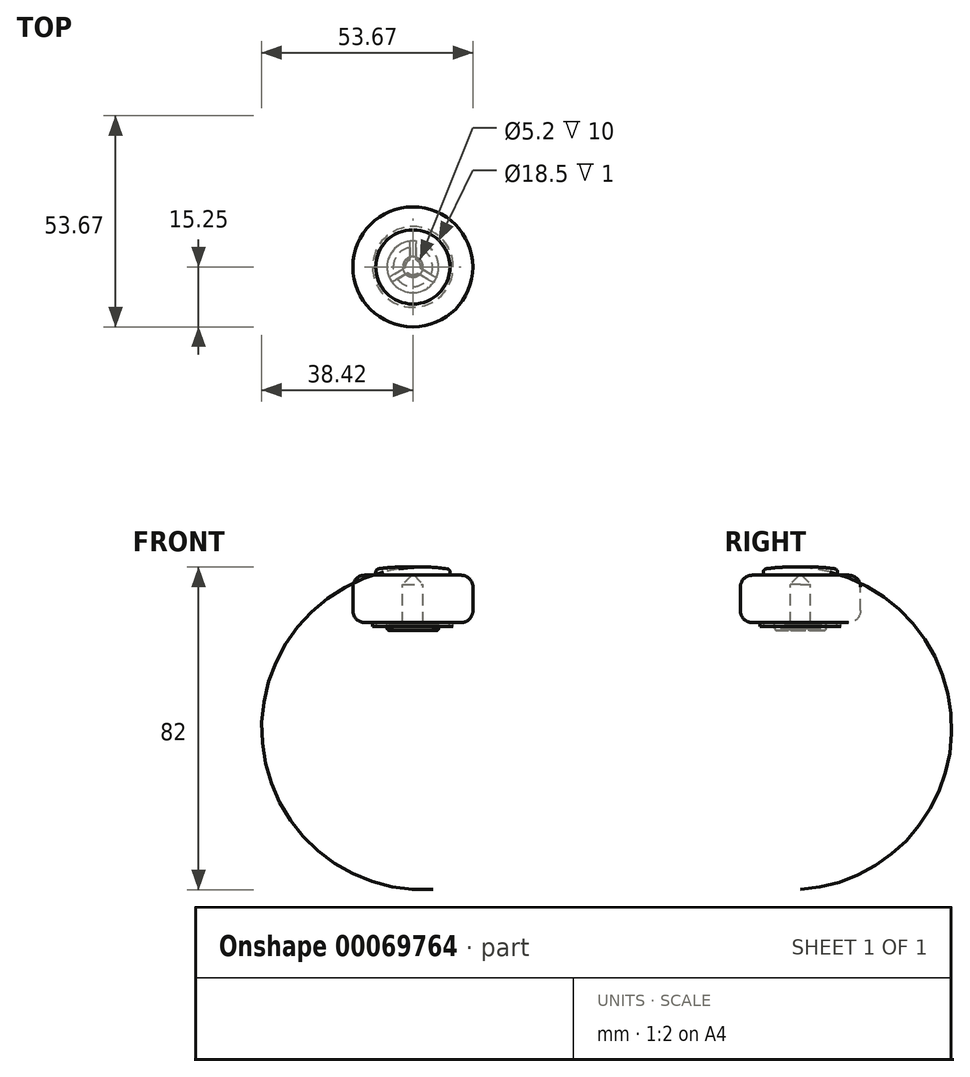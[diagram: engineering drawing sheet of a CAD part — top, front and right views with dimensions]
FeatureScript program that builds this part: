
annotation { "Feature Type Name" : "Feature", "Feature Type Description" : "" }
export const myFeature = defineFeature(function(context is Context, id is Id, definition is map)
    precondition{}
    {
        {
            var Q0;
            Q0=qCreatedBy(makeId("Right.planeOp"),FACE);
            var sketch = newSketch(context, id + "F0", { "sketchPlane" : qUnion([Q0])});
            skLineSegment(sketch, "E0", {"start": v(0, 18.3) * mm, "end": v(0, -9.78) * mm, "construction": true});
            skLineSegment(sketch, "E1", {"start": v(9.43, 2.55) * mm, "end": v(15.25, 2.55) * mm});
            skLineSegment(sketch, "E2", {"start": v(15.25, 2.55) * mm, "end": v(15.25, -9.46) * mm});
            skLineSegment(sketch, "E3", {"start": v(15.25, -9.46) * mm, "end": v(10.25, -9.46) * mm});
            skLineSegment(sketch, "E4", {"start": v(10.25, -9.46) * mm, "end": v(10.25, -10.46) * mm});
            skLineSegment(sketch, "E5", {"start": v(10.25, -10.46) * mm, "end": v(9.25, -10.46) * mm});
            skLineSegment(sketch, "E6", {"start": v(9.25, -10.46) * mm, "end": v(9.25, -9.46) * mm});
            skLineSegment(sketch, "E7", {"start": v(9.25, -9.46) * mm, "end": v(6.55, -9.46) * mm});
            skLineSegment(sketch, "E8", {"start": v(6.55, -9.46) * mm, "end": v(6.55, -11.46) * mm});
            skLineSegment(sketch, "E9", {"start": v(6.55, -11.46) * mm, "end": v(2.55, -11.46) * mm});
            skLineSegment(sketch, "E10", {"start": v(2.55, -11.46) * mm, "end": v(1.95, -9.78) * mm});
            skLineSegment(sketch, "E11", {"start": v(1.95, -9.78) * mm, "end": v(2.6, -9.78) * mm});
            skLineSegment(sketch, "E12", {"start": v(2.6, -9.78) * mm, "end": v(2.6, 0.22) * mm});
            skLineSegment(sketch, "E13", {"start": v(0, 2.82) * mm, "end": v(0, 4.54) * mm});
            skLineSegment(sketch, "E14", {"start": v(2.6, 0.22) * mm, "end": v(0, 2.82) * mm});
            skLineSegment(sketch, "E15", {"start": v(9.43, 2.55) * mm, "end": v(9.43, 4.05) * mm});
            skArc(sketch, "E16", {"start": v(9.43, 4.05) * mm, "mid": v(4.73, 4.57) * mm, "end": v(0, 4.54) * mm});
            skSolve(sketch);
        }
        {
            var Q0;
            Q0 = qSketchRegion(id + "F0", true);
            var Q1;
            Q1=sQuery(id+"F0.wireOp",EDGE,"E0");
            revolve(context, id + "F1", {"entities" : qUnion([Q0]), "axis" : qUnion([Q1]), "revolveType" : RevolveType.FULL});
        }
        {
            var Q0;
            Q0=makeQuery(id+"F1.opRevolve","SWEPT_FACE",FACE,{"disambiguationData":[OSD([sQuery(id+"F0.wireOp",EDGE,"E9")])]});
            var sketch = newSketch(context, id + "F2", { "sketchPlane" : qUnion([Q0])});
            skArc(sketch, "E17", {"start": v(-0.7, -6.51) * mm, "mid": v(0.05, -6.55) * mm, "end": v(0.8, -6.5) * mm});
            skArc(sketch, "E18", {"start": v(-0.7, -1.66) * mm, "mid": v(0.06, -1.8) * mm, "end": v(0.8, -1.61) * mm});
            skLineSegment(sketch, "E19", {"start": v(0.8, -1.61) * mm, "end": v(0.8, -6.5) * mm});
            skLineSegment(sketch, "E20", {"start": v(-0.7, -1.66) * mm, "end": v(-0.7, -6.51) * mm});
            skLineSegment(sketch, "E21.1.0", {"start": v(-1.8, 0.11) * mm, "end": v(-6.03, 2.56) * mm});
            skArc(sketch, "E21.1.1", {"start": v(-5.3, 3.86) * mm, "mid": v(-5.7, 3.23) * mm, "end": v(-6.03, 2.56) * mm});
            skLineSegment(sketch, "E21.1.2", {"start": v(-1.09, 1.43) * mm, "end": v(-5.3, 3.86) * mm});
            skArc(sketch, "E21.1.3", {"start": v(-1.09, 1.43) * mm, "mid": v(-1.59, 0.85) * mm, "end": v(-1.8, 0.11) * mm});
            skLineSegment(sketch, "E21.2.0", {"start": v(1, 1.5) * mm, "end": v(5.23, 3.94) * mm});
            skArc(sketch, "E21.2.1", {"start": v(5.99, 2.65) * mm, "mid": v(5.65, 3.32) * mm, "end": v(5.23, 3.94) * mm});
            skLineSegment(sketch, "E21.2.2", {"start": v(1.78, 0.22) * mm, "end": v(5.99, 2.65) * mm});
            skArc(sketch, "E21.2.3", {"start": v(1.78, 0.22) * mm, "mid": v(1.53, 0.95) * mm, "end": v(1, 1.5) * mm});
            skLineSegment(sketch, "E21.anchor1", {"start": v(0, 0) * mm, "end": v(0.8, -6.5) * mm, "construction": true});
            skLineSegment(sketch, "E21.anchor2", {"start": v(0, 0) * mm, "end": v(5.23, 3.94) * mm, "construction": true});
            skSolve(sketch);
        }
        {
            var Q0;
            Q0 = qSketchRegion(id + "F2", true);
            var Q1;
            Q1=makeQuery(id+"F1.opRevolve","SWEPT_FACE",FACE,{"disambiguationData":[OSD([sQuery(id+"F0.wireOp",EDGE,"E11")])]});
            extrude(context, id + "F3", {"entities" : qUnion([Q0]), "operationType" : NewBodyOperationType.REMOVE, "endBound" : BoundingType.UP_TO_SURFACE, "oppositeDirection" : true, "endBoundEntityFace" : qUnion([Q1]), "depth" : 25 * mm});
        }
        {
            var Q0;
            {var subQ0=sQuery(id+"F0.wireOp",EDGE,"E8");var subQ1=sQuery(id+"F0.wireOp",EDGE,"E9");Q0=makeQuery(id+"F3.boolean.opBoolean","SPLIT",EDGE,{"disambiguationData":[TD([makeQuery(id+"F3.opExtrude","SWEPT_FACE",FACE,{"disambiguationData":[OSD([sQuery(id+"F2.wireOp",EDGE,"E20")])]})])],"derivedFrom":makeQuery(id+"F1.opRevolve","SWEPT_EDGE",EDGE,{"disambiguationData":[OSD([subQ0,subQ1])]})});}
            var Q1;
            {var subQ0=sQuery(id+"F0.wireOp",EDGE,"E8");var subQ1=sQuery(id+"F0.wireOp",EDGE,"E9");Q1=makeQuery(id+"F3.boolean.opBoolean","SPLIT",EDGE,{"disambiguationData":[TD([makeQuery(id+"F3.opExtrude","SWEPT_FACE",FACE,{"disambiguationData":[OSD([sQuery(id+"F2.wireOp",EDGE,"E19")])]})])],"derivedFrom":makeQuery(id+"F1.opRevolve","SWEPT_EDGE",EDGE,{"disambiguationData":[OSD([subQ0,subQ1])]})});}
            var Q2;
            {var subQ0=sQuery(id+"F0.wireOp",EDGE,"E8");var subQ1=sQuery(id+"F0.wireOp",EDGE,"E9");Q2=makeQuery(id+"F3.boolean.opBoolean","SPLIT",EDGE,{"disambiguationData":[TD([makeQuery(id+"F3.opExtrude","SWEPT_FACE",FACE,{"disambiguationData":[OSD([sQuery(id+"F2.wireOp",EDGE,"E21.1.2")])]})])],"derivedFrom":makeQuery(id+"F1.opRevolve","SWEPT_EDGE",EDGE,{"disambiguationData":[OSD([subQ0,subQ1])]})});}
            fillet(context, id + "F4", {"entities" : qUnion([Q0, Q1, Q2]), "radius" : 0.5 * mm, "tangentPropagation" : true, "allowEdgeOverflow" : false});
        }
        {
            var Q0;
            Q0=makeQuery(id+"F1.opRevolve","SWEPT_EDGE",EDGE,{"disambiguationData":[OSD([sQuery(id+"F0.wireOp",EDGE,"E2"),sQuery(id+"F0.wireOp",EDGE,"E3")])]});
            var Q1;
            Q1=makeQuery(id+"F1.opRevolve","SWEPT_EDGE",EDGE,{"disambiguationData":[OSD([sQuery(id+"F0.wireOp",EDGE,"E1"),sQuery(id+"F0.wireOp",EDGE,"E2")])]});
            fillet(context, id + "F5", {"entities" : qUnion([Q0, Q1]), "radius" : 3 * mm, "tangentPropagation" : true, "allowEdgeOverflow" : false});
        }
        {
            var Q0;
            Q0=makeQuery(id+"F1.opRevolve","SWEPT_EDGE",EDGE,{"disambiguationData":[OSD([sQuery(id+"F0.wireOp",EDGE,"E15"),sQuery(id+"F0.wireOp",EDGE,"E16")])]});
            fillet(context, id + "F6", {"entities" : qUnion([Q0]), "radius" : 0.8 * mm, "tangentPropagation" : true, "allowEdgeOverflow" : false});
        }
        {
            var Q0;
            Q0=makeQuery(id+"F3.boolean.opBoolean","SPLIT",FACE,{"disambiguationData":[TD([makeQuery(id+"F3.opExtrude","SWEPT_FACE",FACE,{"disambiguationData":[OSD([sQuery(id+"F2.wireOp",EDGE,"E21.1.2")])]})])],"derivedFrom":makeQuery(id+"F1.opRevolve","SWEPT_FACE",FACE,{"disambiguationData":[OSD([sQuery(id+"F0.wireOp",EDGE,"E9")])]})});
            var sketch = newSketch(context, id + "F7", { "sketchPlane" : qUnion([Q0])});
            skCircle(sketch, "E22", {"center": v(0, 0) * mm, "radius": 5 * mm});
            skSolve(sketch);
        }
        {
            var Q0;
            Q0 = qSketchRegion(id + "F7", true);
            extrude(context, id + "F8", {"entities" : qUnion([Q0]), "operationType" : NewBodyOperationType.REMOVE, "oppositeDirection" : true, "depth" : .5 * mm});
        }
    });
